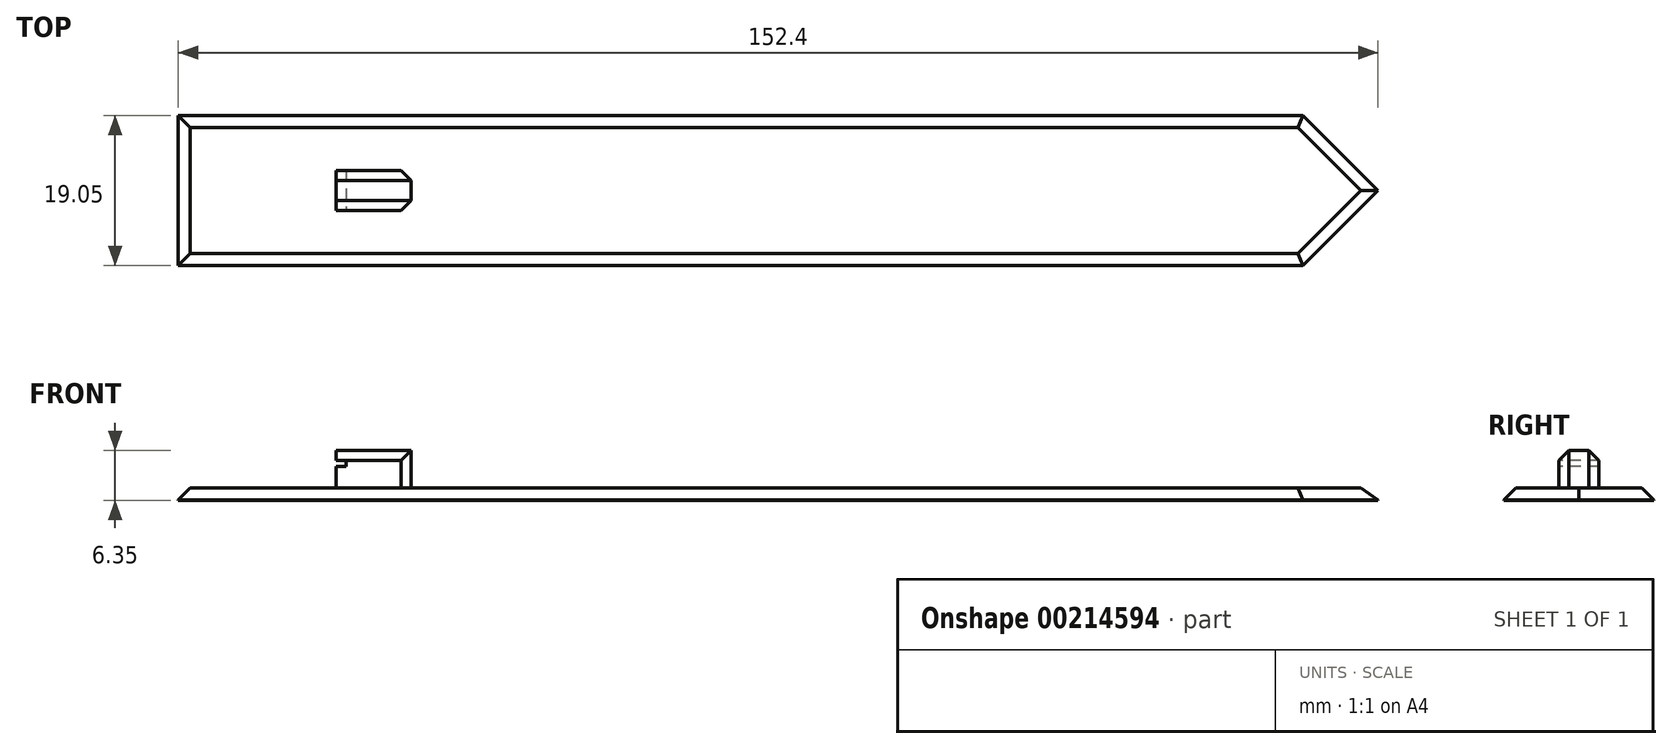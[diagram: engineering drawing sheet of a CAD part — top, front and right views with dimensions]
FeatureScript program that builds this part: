
annotation { "Feature Type Name" : "Feature", "Feature Type Description" : "" }
export const myFeature = defineFeature(function(context is Context, id is Id, definition is map)
    precondition{}
    {
        {
            var Q0;
            Q0=qCreatedBy(makeId("Top.planeOp"),FACE);
            var sketch = newSketch(context, id + "F0", { "sketchPlane" : qUnion([Q0])});
            skLineSegment(sketch, "E0.bottom", {"start": v(-73.7, 32.17) * mm, "end": v(78.7, 32.17) * mm});
            skLineSegment(sketch, "E0.top", {"start": v(-73.7, 13.12) * mm, "end": v(78.7, 13.12) * mm});
            skLineSegment(sketch, "E0.left", {"start": v(-73.7, 32.17) * mm, "end": v(-73.7, 13.12) * mm});
            skLineSegment(sketch, "E0.right", {"start": v(78.7, 32.17) * mm, "end": v(78.7, 13.12) * mm});
            skSolve(sketch);
        }
        {
            var Q0;
            Q0=makeQuery(id+"F0.imprint","IMPRINT",FACE,{"disambiguationData":[TD([[makeQuery(id+"F0.imprint","IMPRINT",EDGE,{"derivedFrom":sQuery(id+"F0.wireOp",EDGE,"E0.bottom")}),-1.0]])]});
            extrude(context, id + "F1", {"entities" : qUnion([Q0]), "oppositeDirection" : true, "depth" : 1.59 * mm});
        }
        {
            var Q0;
            Q0=makeQuery(id+"F1.opExtrude","SWEPT_EDGE",EDGE,{"disambiguationData":[OSD([sQuery(id+"F0.wireOp",EDGE,"E0.top"),sQuery(id+"F0.wireOp",EDGE,"E0.right")])]});
            var Q1;
            Q1=makeQuery(id+"F1.opExtrude","SWEPT_EDGE",EDGE,{"disambiguationData":[OSD([sQuery(id+"F0.wireOp",EDGE,"E0.bottom"),sQuery(id+"F0.wireOp",EDGE,"E0.right")])]});
            chamfer(context, id + "F2", {"entities" : qUnion([Q0, Q1]), "width" : 9.52 * mm, "tangentPropagation" : true});
        }
        {
            var Q0;
            Q0=makeQuery(id+"F1.opExtrude","CAP_FACE",FACE,{"disambiguationData":[OSD([sQuery(id+"F0.wireOp",EDGE,"E0.bottom"),sQuery(id+"F0.wireOp",EDGE,"E0.top"),sQuery(id+"F0.wireOp",EDGE,"E0.left"),sQuery(id+"F0.wireOp",EDGE,"E0.right")])],"isStart":true});
            var sketch = newSketch(context, id + "F3", { "sketchPlane" : qUnion([Q0])});
            skLineSegment(sketch, "E1.bottom", {"start": v(-53.64, 25.19) * mm, "end": v(-44.11, 25.19) * mm});
            skLineSegment(sketch, "E1.top", {"start": v(-53.64, 20.1) * mm, "end": v(-44.11, 20.1) * mm});
            skLineSegment(sketch, "E1.left", {"start": v(-53.64, 25.19) * mm, "end": v(-53.64, 20.1) * mm});
            skLineSegment(sketch, "E1.right", {"start": v(-44.11, 25.19) * mm, "end": v(-44.11, 20.1) * mm});
            skSolve(sketch);
        }
        {
            var Q0;
            Q0=makeQuery(id+"F3.imprint","IMPRINT",FACE,{"disambiguationData":[TD([[makeQuery(id+"F3.imprint","IMPRINT",EDGE,{"derivedFrom":sQuery(id+"F3.wireOp",EDGE,"E1.bottom")}),-1.0]])]});
            extrude(context, id + "F4", {"entities" : qUnion([Q0]), "operationType" : NewBodyOperationType.ADD, "depth" : 4.76 * mm});
        }
        {
            var Q0;
            Q0=makeQuery(id+"F4.opExtrude","SWEPT_EDGE",EDGE,{"disambiguationData":[OSD([sQuery(id+"F3.wireOp",EDGE,"E1.top"),sQuery(id+"F3.wireOp",EDGE,"E1.right")])]});
            var Q1;
            Q1=makeQuery(id+"F4.opExtrude","SWEPT_EDGE",EDGE,{"disambiguationData":[OSD([sQuery(id+"F3.wireOp",EDGE,"E1.bottom"),sQuery(id+"F3.wireOp",EDGE,"E1.right")])]});
            var Q2;
            Q2=makeQuery(id+"F4.opExtrude","CAP_EDGE",EDGE,{"disambiguationData":[OSD([sQuery(id+"F3.wireOp",EDGE,"E1.bottom")])],"isStart":false});
            var Q3;
            Q3=makeQuery(id+"F4.opExtrude","CAP_EDGE",EDGE,{"disambiguationData":[OSD([sQuery(id+"F3.wireOp",EDGE,"E1.top")])],"isStart":false});
            chamfer(context, id + "F5", {"entities" : qUnion([Q0, Q1, Q2, Q3]), "width" : 1.27 * mm, "tangentPropagation" : true});
        }
        {
            var Q0;
            Q0=makeQuery(id+"F4.opExtrude","SWEPT_FACE",FACE,{"disambiguationData":[OSD([sQuery(id+"F3.wireOp",EDGE,"E1.left")])]});
            var sketch = newSketch(context, id + "F6", { "sketchPlane" : qUnion([Q0])});
            skLineSegment(sketch, "E2.bottom", {"start": v(-25.19, 3.5) * mm, "end": v(-20.08, 3.5) * mm});
            skLineSegment(sketch, "E2.top", {"start": v(-25.19, 2.73) * mm, "end": v(-20.08, 2.73) * mm});
            skLineSegment(sketch, "E2.left", {"start": v(-25.19, 3.5) * mm, "end": v(-25.19, 2.73) * mm});
            skLineSegment(sketch, "E2.right", {"start": v(-20.08, 3.5) * mm, "end": v(-20.08, 2.73) * mm});
            skSolve(sketch);
        }
        {
            var Q0;
            {var subQ0=sQuery(id+"F6.wireOp",EDGE,"E2.left");Q0=makeQuery(id+"F6.imprint","IMPRINT",FACE,{"disambiguationData":[TD([[makeQuery(id+"F6.imprint","IMPRINT",EDGE,{"derivedFrom":subQ0}),1.0]])]});}
            extrude(context, id + "F7", {"entities" : qUnion([Q0]), "operationType" : NewBodyOperationType.REMOVE, "oppositeDirection" : true, "depth" : 1.27 * mm});
        }
        {
            var Q0;
            Q0=makeQuery(id+"F1.opExtrude","CAP_EDGE",EDGE,{"disambiguationData":[OSD([sQuery(id+"F0.wireOp",EDGE,"E0.top")])],"isStart":true});
            chamfer(context, id + "F8", {"entities" : qUnion([Q0]), "width" : 1.52 * mm, "tangentPropagation" : true});
        }
        {
            var Q0;
            {var subQ0=sQuery(id+"F0.wireOp",EDGE,"E0.right");var subQ1=sQuery(id+"F0.wireOp",EDGE,"E0.top");Q0=makeQuery(id+"F2.opChamfer","BLEND_EDGE",EDGE,{"blendedFrom":[makeQuery(id+"F1.opExtrude","SWEPT_EDGE",EDGE,{"disambiguationData":[OSD([subQ1,subQ0])]}),makeQuery(id+"F1.opExtrude","CAP_FACE",FACE,{"disambiguationData":[OSD([sQuery(id+"F0.wireOp",EDGE,"E0.bottom"),subQ1,sQuery(id+"F0.wireOp",EDGE,"E0.left"),subQ0])],"isStart":true})],"blendedInto":[makeQuery(id+"F1.opExtrude","CAP_FACE",FACE,{"disambiguationData":[OSD([sQuery(id+"F0.wireOp",EDGE,"E0.bottom"),subQ1,sQuery(id+"F0.wireOp",EDGE,"E0.left"),subQ0])],"isStart":true})]});}
            var Q1;
            {var subQ0=sQuery(id+"F0.wireOp",EDGE,"E0.right");var subQ1=sQuery(id+"F0.wireOp",EDGE,"E0.bottom");Q1=makeQuery(id+"F2.opChamfer","BLEND_EDGE",EDGE,{"blendedFrom":[makeQuery(id+"F1.opExtrude","SWEPT_EDGE",EDGE,{"disambiguationData":[OSD([subQ1,subQ0])]}),makeQuery(id+"F1.opExtrude","CAP_FACE",FACE,{"disambiguationData":[OSD([subQ1,sQuery(id+"F0.wireOp",EDGE,"E0.top"),sQuery(id+"F0.wireOp",EDGE,"E0.left"),subQ0])],"isStart":true})],"blendedInto":[makeQuery(id+"F1.opExtrude","CAP_FACE",FACE,{"disambiguationData":[OSD([subQ1,sQuery(id+"F0.wireOp",EDGE,"E0.top"),sQuery(id+"F0.wireOp",EDGE,"E0.left"),subQ0])],"isStart":true})]});}
            var Q2;
            Q2=makeQuery(id+"F1.opExtrude","CAP_EDGE",EDGE,{"disambiguationData":[OSD([sQuery(id+"F0.wireOp",EDGE,"E0.bottom")])],"isStart":true});
            chamfer(context, id + "F9", {"entities" : qUnion([Q0, Q1, Q2]), "width" : 1.52 * mm, "tangentPropagation" : true});
        }
        {
            var Q0;
            Q0=makeQuery(id+"F1.opExtrude","CAP_EDGE",EDGE,{"disambiguationData":[OSD([sQuery(id+"F0.wireOp",EDGE,"E0.left")])],"isStart":true});
            chamfer(context, id + "F10", {"entities" : qUnion([Q0]), "width" : 1.52 * mm, "tangentPropagation" : true});
        }
    });
